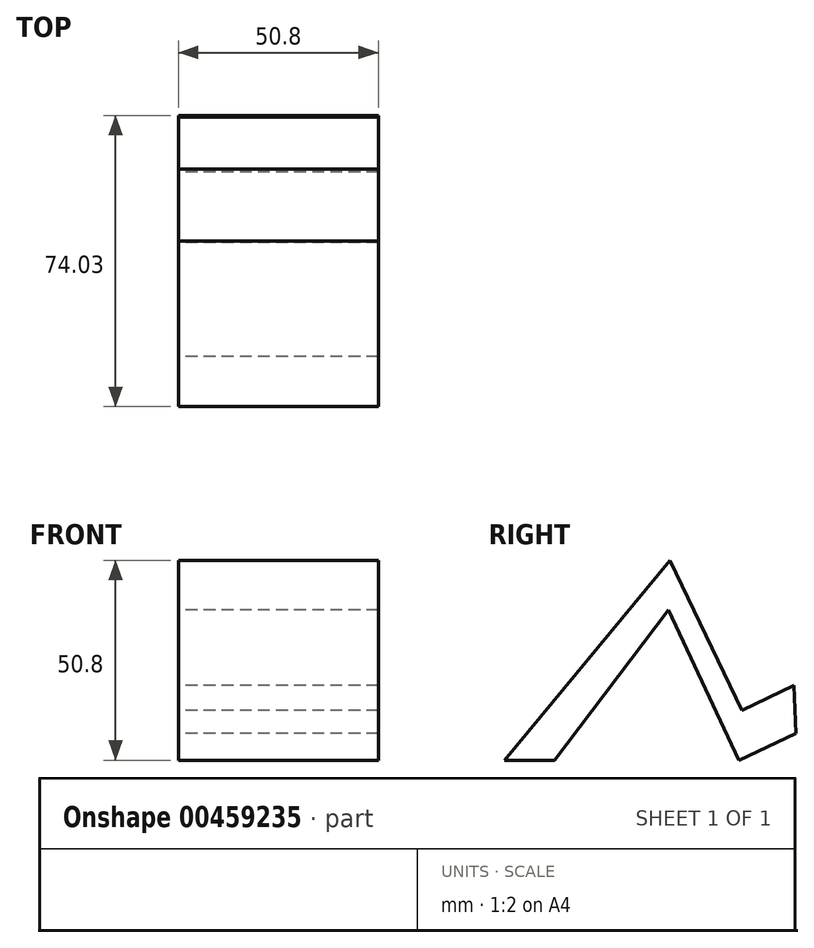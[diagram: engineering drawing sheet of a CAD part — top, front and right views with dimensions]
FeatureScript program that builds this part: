
annotation { "Feature Type Name" : "Feature", "Feature Type Description" : "" }
export const myFeature = defineFeature(function(context is Context, id is Id, definition is map)
    precondition{}
    {
        {
            var Q0;
            Q0=qCreatedBy(makeId("Right.planeOp"),FACE);
            var sketch = newSketch(context, id + "F0", { "sketchPlane" : qUnion([Q0])});
            skLineSegment(sketch, "E0", {"start": v(0, 0) * mm, "end": v(28.98, 38.1) * mm});
            skLineSegment(sketch, "E1", {"start": v(28.98, 38.1) * mm, "end": v(46.95, 0) * mm});
            skLineSegment(sketch, "E2", {"start": v(47.68, 12.68) * mm, "end": v(29.34, 50.8) * mm});
            skLineSegment(sketch, "E3", {"start": v(29.34, 50.8) * mm, "end": v(-12.7, 0) * mm});
            skLineSegment(sketch, "E4", {"start": v(-12.7, 0) * mm, "end": v(0, 0) * mm});
            skLineSegment(sketch, "E5", {"start": v(28.98, 38.1) * mm, "end": v(29.34, 50.8) * mm});
            skLineSegment(sketch, "E6", {"start": v(46.95, 0) * mm, "end": v(47.68, 12.68) * mm});
            skLineSegment(sketch, "E7", {"start": v(47.68, 12.68) * mm, "end": v(60.89, 19.03) * mm});
            skLineSegment(sketch, "E8", {"start": v(46.95, 0) * mm, "end": v(61.33, 6.78) * mm});
            skLineSegment(sketch, "E9", {"start": v(61.33, 6.78) * mm, "end": v(60.89, 19.03) * mm});
            skSolve(sketch);
        }
        {
            var Q0;
            Q0=makeQuery(id+"F0.imprint","IMPRINT",FACE,{"disambiguationData":[TD([[makeQuery(id+"F0.imprint","IMPRINT",EDGE,{"derivedFrom":sQuery(id+"F0.wireOp",EDGE,"E6")}),-1.0]])]});
            extrude(context, id + "F1", {"entities" : qUnion([Q0]), "endBound" : BoundingType.SYMMETRIC, "depth" : 50.8 * mm});
        }
        {
            var Q0;
            Q0=makeQuery(id+"F0.imprint","IMPRINT",FACE,{"disambiguationData":[TD([[makeQuery(id+"F0.imprint","IMPRINT",EDGE,{"derivedFrom":sQuery(id+"F0.wireOp",EDGE,"E1")}),1.0]])]});
            extrude(context, id + "F2", {"entities" : qUnion([Q0]), "operationType" : NewBodyOperationType.ADD, "endBound" : BoundingType.SYMMETRIC, "depth" : 50.8 * mm});
        }
        {
            var Q0;
            Q0=makeQuery(id+"F0.imprint","IMPRINT",FACE,{"disambiguationData":[TD([[makeQuery(id+"F0.imprint","IMPRINT",EDGE,{"derivedFrom":sQuery(id+"F0.wireOp",EDGE,"E0")}),1.0]])]});
            extrude(context, id + "F3", {"entities" : qUnion([Q0]), "operationType" : NewBodyOperationType.ADD, "endBound" : BoundingType.SYMMETRIC, "depth" : 50.8 * mm});
        }
    });
